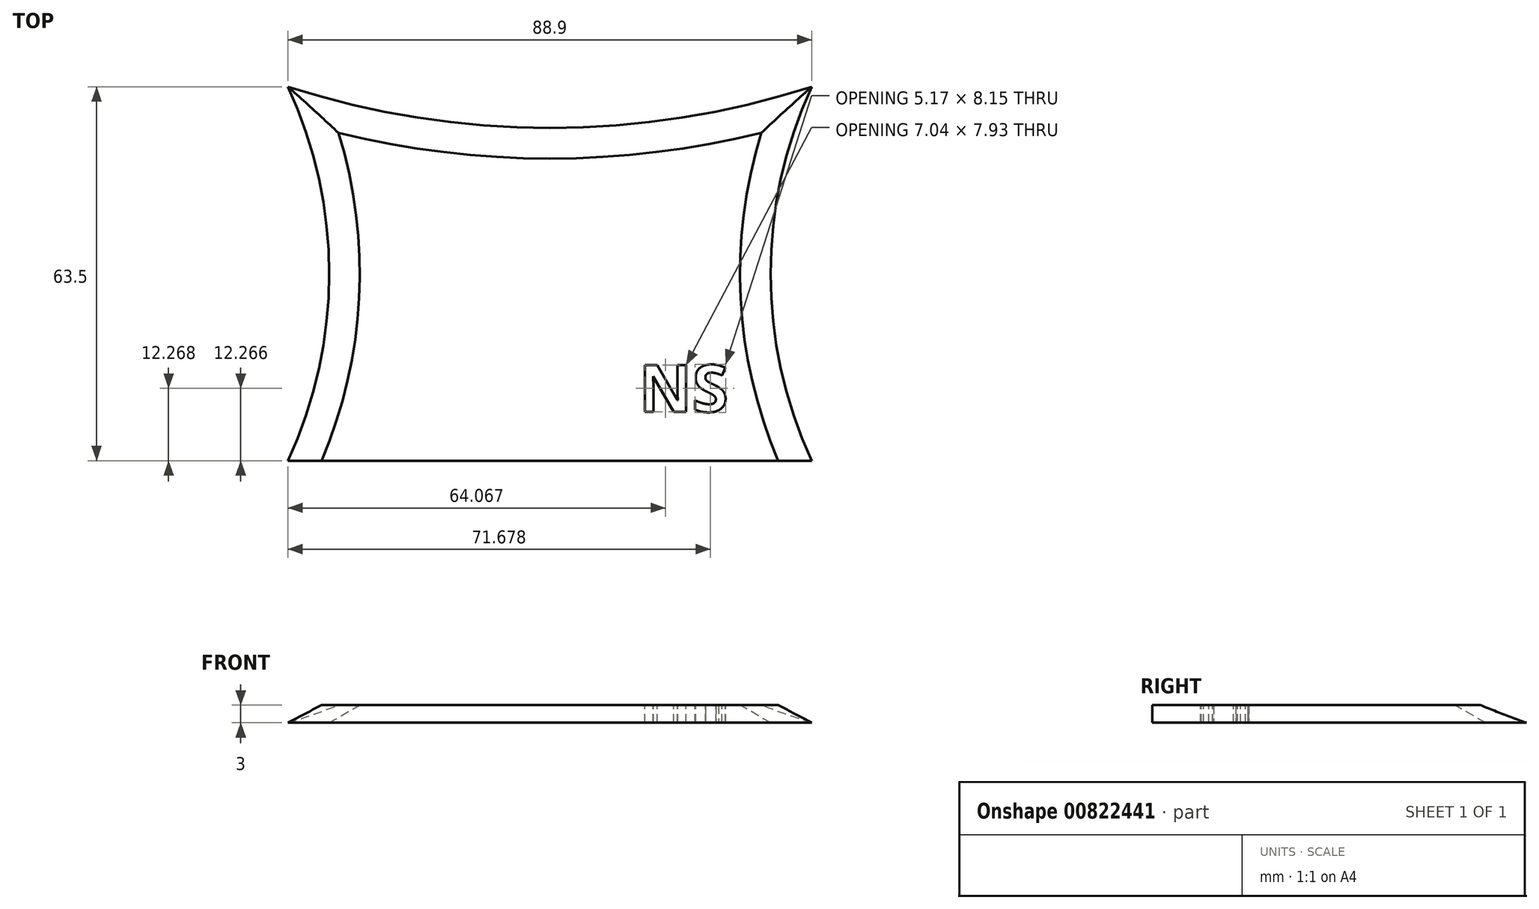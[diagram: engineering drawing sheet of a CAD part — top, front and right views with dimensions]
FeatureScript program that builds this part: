
annotation { "Feature Type Name" : "Feature", "Feature Type Description" : "" }
export const myFeature = defineFeature(function(context is Context, id is Id, definition is map)
    precondition{}
    {
        {
            var Q0;
            Q0=qCreatedBy(makeId("Top.planeOp"),FACE);
            var sketch = newSketch(context, id + "F0", { "sketchPlane" : qUnion([Q0])});
            skLineSegment(sketch, "E0.bottom", {"start": v(0, 0) * mm, "end": v(88.9, 0) * mm});
            skLineSegment(sketch, "E1", {"start": v(7, 0) * mm, "end": v(7, 56.5) * mm});
            skLineSegment(sketch, "E2", {"start": v(81.9, 0) * mm, "end": v(81.9, 56.5) * mm});
            skLineSegment(sketch, "E3", {"start": v(7, 56.5) * mm, "end": v(81.9, 56.5) * mm});
            skPoint(sketch, "E4", {"position": v(44.45, 56.5) * mm});
            skPoint(sketch, "E5", {"position": v(7, 31.75) * mm});
            skPoint(sketch, "E6", {"position": v(81.9, 31.75) * mm});
            skArc(sketch, "E7", {"start": v(0, 0) * mm, "mid": v(7, 31.75) * mm, "end": v(0, 63.5) * mm});
            skArc(sketch, "E8", {"start": v(0, 63.5) * mm, "mid": v(44.45, 56.5) * mm, "end": v(88.9, 63.5) * mm});
            skArc(sketch, "E9", {"start": v(88.9, 63.5) * mm, "mid": v(81.9, 31.75) * mm, "end": v(88.9, 0) * mm});
            skPoint(sketch, "E10.trimOffspring.end.orphan", {"position": v(7, 63.5) * mm});
            skPoint(sketch, "E11.orphan", {"position": v(0, 56.5) * mm});
            skPoint(sketch, "E12.orphan", {"position": v(81.9, 63.5) * mm});
            skPoint(sketch, "E13.orphan", {"position": v(88.9, 56.5) * mm});
            skSolve(sketch);
        }
        {
            var Q0;
            Q0=makeQuery(id+"F0.imprint","IMPRINT",FACE,{"disambiguationData":[TD([[makeQuery(id+"F0.imprint","IMPRINT",EDGE,{"derivedFrom":sQuery(id+"F0.wireOp",EDGE,"E0.bottom")}),1.0]])]});
            var Q1;
            {var subQ1=sQuery(id+"F0.wireOp",EDGE,"E0.bottom");var subQ5=sQuery(id+"F0.wireOp",EDGE,"E1");var subQ8=makeQuery(id+"F0.imprint","INTERSECT",VERTEX,{"derivedFrom":[subQ1,subQ5]});Q1=makeQuery(id+"F0.imprint","IMPRINT",FACE,{"disambiguationData":[TD([[makeQuery(id+"F0.imprint","IMPRINT",EDGE,{"disambiguationData":[TD([[subQ8,-1.0]])],"derivedFrom":subQ1}),1.0]])]});}
            var Q2;
            {var subQ0=sQuery(id+"F0.wireOp",EDGE,"E3");var subQ1=sQuery(id+"F0.wireOp",EDGE,"E2");var subQ2=makeQuery(id+"F0.imprint","INTERSECT",VERTEX,{"derivedFrom":[subQ1,subQ0]});Q2=makeQuery(id+"F0.imprint","IMPRINT",FACE,{"disambiguationData":[TD([[makeQuery(id+"F0.imprint","IMPRINT",EDGE,{"disambiguationData":[TD([[subQ2,1.0]])],"derivedFrom":subQ1}),-1.0]])]});}
            var Q3;
            {var subQ0=sQuery(id+"F0.wireOp",EDGE,"E3");var subQ1=sQuery(id+"F0.wireOp",EDGE,"E1");var subQ2=makeQuery(id+"F0.imprint","INTERSECT",VERTEX,{"derivedFrom":[subQ1,subQ0]});Q3=makeQuery(id+"F0.imprint","IMPRINT",FACE,{"disambiguationData":[TD([[makeQuery(id+"F0.imprint","IMPRINT",EDGE,{"disambiguationData":[TD([[subQ2,1.0]])],"derivedFrom":subQ1}),1.0]])]});}
            extrude(context, id + "F1", {"entities" : qUnion([Q0, Q1, Q2, Q3]), "depth" : 3 * mm, "offsetDistance" : 25 * mm});
        }
        {
            var Q0;
            Q0=makeQuery(id+"F1.opExtrude","CAP_EDGE",EDGE,{"disambiguationData":[OSD([sQuery(id+"F0.wireOp",EDGE,"E9")])],"isStart":false});
            var Q1;
            Q1=makeQuery(id+"F1.opExtrude","CAP_EDGE",EDGE,{"disambiguationData":[OSD([sQuery(id+"F0.wireOp",EDGE,"E8")])],"isStart":false});
            var Q2;
            Q2=makeQuery(id+"F1.opExtrude","CAP_EDGE",EDGE,{"disambiguationData":[OSD([sQuery(id+"F0.wireOp",EDGE,"E7")])],"isStart":false});
            chamfer(context, id + "F2", {"entities" : qUnion([Q0, Q1, Q2]), "chamferType" : ChamferType.OFFSET_ANGLE, "width" : 3 * mm, "oppositeDirection" : false, "angle" : 60 * degree, "tangentPropagation" : true});
        }
        {
            var Q0;
            Q0=qCreatedBy(makeId("Top.planeOp"),FACE);
            var sketch = newSketch(context, id + "F3", { "sketchPlane" : qUnion([Q0])});
            skText(sketch, "E14", { "text": "NS", "fontName": "OpenSans-Bold.ttf"});
            const initialGuessF3  = {"E14": [0.05955, 0.0083, 1, 0, 0.008]};
            skSetInitialGuess(sketch, initialGuessF3);
            skSolve(sketch);
        }
        {
            var Q0;
            Q0 = qSketchRegion(id + "F3", true);
            extrude(context, id + "F4", {"entities" : qUnion([Q0]), "operationType" : NewBodyOperationType.REMOVE, "endBound" : BoundingType.SYMMETRIC, "oppositeDirection" : true, "depth" : 25 * mm, "offsetDistance" : 25 * mm});
        }
    });
